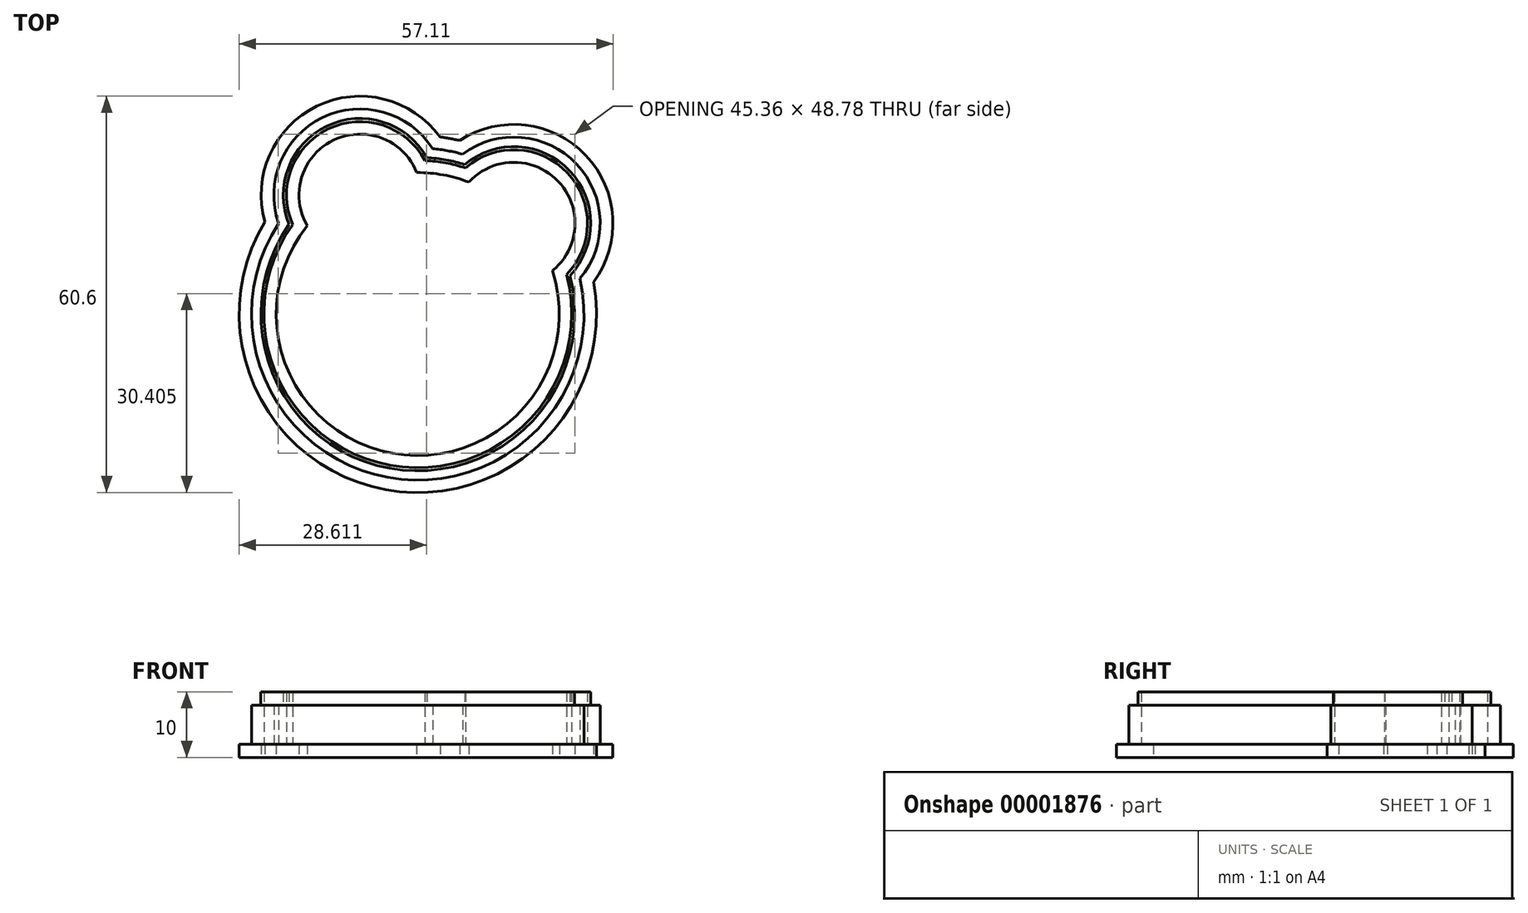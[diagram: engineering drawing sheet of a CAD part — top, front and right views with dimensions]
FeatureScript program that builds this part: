
annotation { "Feature Type Name" : "Feature", "Feature Type Description" : "" }
export const myFeature = defineFeature(function(context is Context, id is Id, definition is map)
    precondition{}
    {
        {
            var Q0;
            Q0=qCreatedBy(makeId("Top.planeOp"),FACE);
            var sketch = newSketch(context, id + "F0", { "sketchPlane" : qUnion([Q0])});
            skArc(sketch, "E0", {"start": v(-14.84, 13.4) * mm, "mid": v(-3.6, -19.67) * mm, "end": v(18.63, 7.28) * mm});
            skArc(sketch, "E1", {"start": v(-1.34, 19.95) * mm, "mid": v(-12.18, 25.1) * mm, "end": v(-14.84, 13.4) * mm});
            skArc(sketch, "E2", {"start": v(18.63, 7.28) * mm, "mid": v(20.28, 19.16) * mm, "end": v(8.33, 18.18) * mm});
            skArc(sketch, "E3.trimOffspring", {"start": v(8.33, 18.18) * mm, "mid": v(3.6, 19.67) * mm, "end": v(-1.34, 19.95) * mm});
            skSolve(sketch);
        }
        {
            var Q0;
            Q0=qCreatedBy(makeId("Right.planeOp"),FACE);
            cPlane(context, id + "F1", {"entities" : qUnion([Q0]), "cplaneType" : CPlaneType.OFFSET, "offset" : 8 * mm, "width" : 150 * mm, "height" : 150 * mm});
        }
        {
            var Q0;
            Q0=qCreatedBy(id+"F1.planeOp",FACE);
            var sketch = newSketch(context, id + "F2", { "sketchPlane" : qUnion([Q0])});
            skLineSegment(sketch, "E4.2", {"start": v(22.6, 6) * mm, "end": v(24.1, 6) * mm});
            skLineSegment(sketch, "E4.4", {"start": v(22.1, 8) * mm, "end": v(22.1, 0) * mm});
            skLineSegment(sketch, "E4.7", {"start": v(26.1, -2) * mm, "end": v(26.1, 0) * mm});
            skLineSegment(sketch, "E5", {"start": v(24.1, 6) * mm, "end": v(24.1, 0) * mm});
            skLineSegment(sketch, "E6", {"start": v(24.1, 0) * mm, "end": v(26.1, 0) * mm});
            skLineSegment(sketch, "E7", {"start": v(26.1, -2) * mm, "end": v(20.1, -2) * mm});
            skLineSegment(sketch, "E8", {"start": v(20.1, -2) * mm, "end": v(20.1, 0) * mm});
            skLineSegment(sketch, "E9", {"start": v(20.1, 0) * mm, "end": v(22.1, 0) * mm});
            skLineSegment(sketch, "E10", {"start": v(22.1, 8) * mm, "end": v(22.6, 8) * mm});
            skLineSegment(sketch, "E11", {"start": v(22.6, 8) * mm, "end": v(22.6, 6) * mm});
            skSolve(sketch);
        }
        {
            var Q0;
            Q0=makeQuery(id+"F2.imprint","IMPRINT",FACE,{"disambiguationData":[TD([[makeQuery(id+"F2.imprint","IMPRINT",EDGE,{"derivedFrom":sQuery(id+"F2.wireOp",EDGE,"E4.2")}),-1.0]])]});
            var Q1;
            Q1=sQuery(id+"F0.wireOp",EDGE,"E3.trimOffspring");
            var Q2;
            Q2=sQuery(id+"F0.wireOp",EDGE,"E1");
            var Q3;
            Q3=sQuery(id+"F0.wireOp",EDGE,"E0");
            var Q4;
            Q4=sQuery(id+"F0.wireOp",EDGE,"E2");
            sweep(context, id + "F3", {"profiles" : qUnion([Q0]), "path" : qUnion([Q1, Q2, Q3, Q4])});
        }
    });
